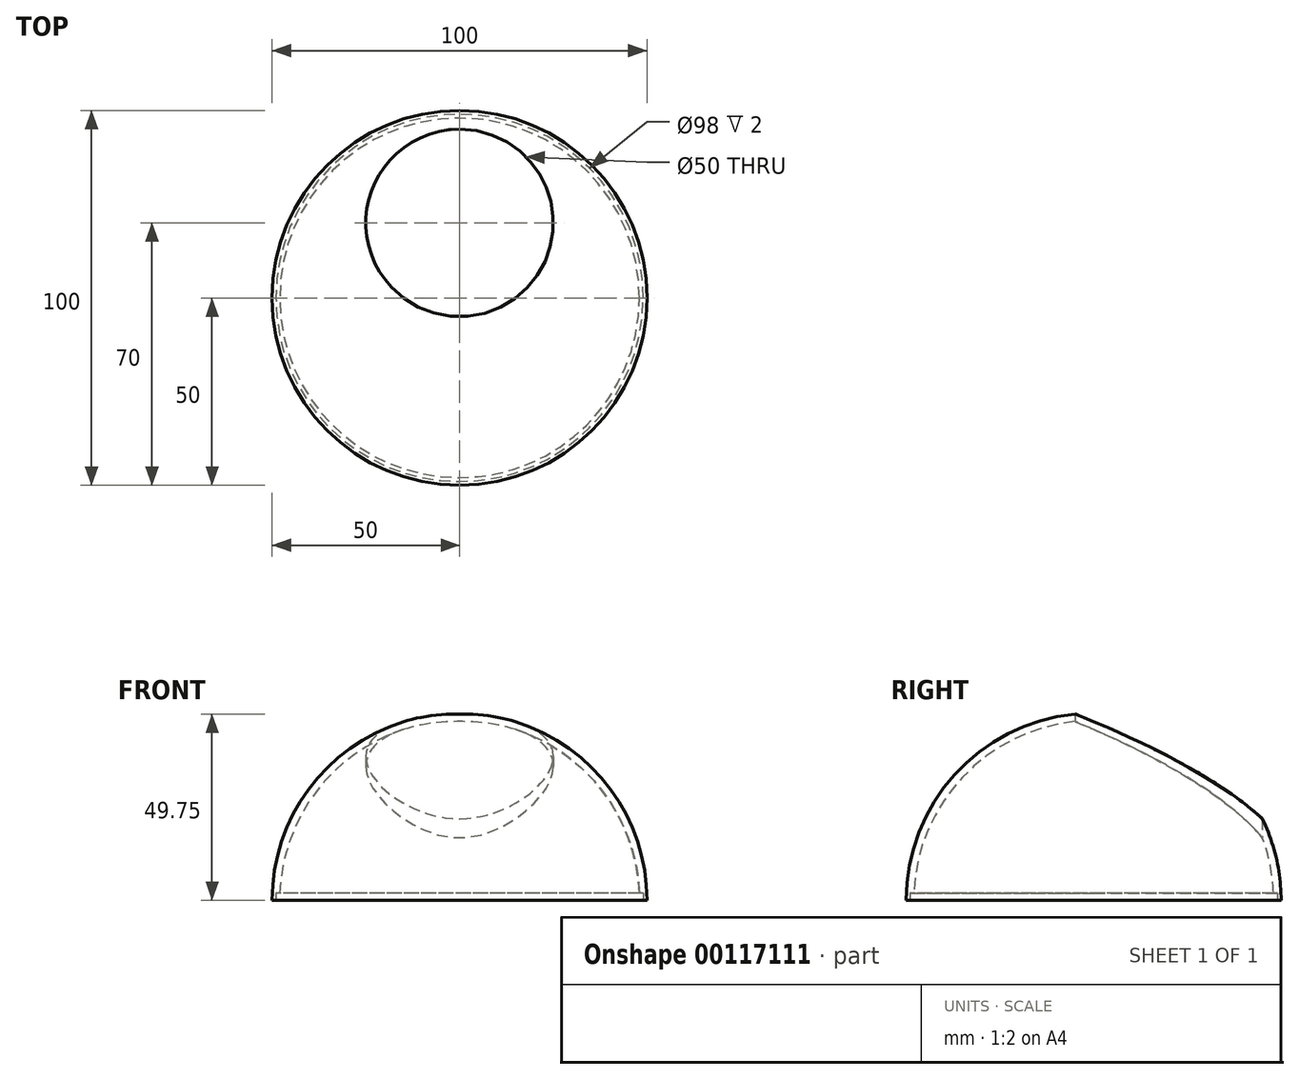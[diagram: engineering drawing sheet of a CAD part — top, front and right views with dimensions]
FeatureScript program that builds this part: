
annotation { "Feature Type Name" : "Feature", "Feature Type Description" : "" }
export const myFeature = defineFeature(function(context is Context, id is Id, definition is map)
    precondition{}
    {
        {
            var Q0;
            Q0=qCreatedBy(makeId("Front.planeOp"),FACE);
            var sketch = newSketch(context, id + "F0", { "sketchPlane" : qUnion([Q0])});
            skLineSegment(sketch, "E0.bottom", {"start": v(0, 0) * mm, "end": v(50, 0) * mm});
            skLineSegment(sketch, "E0.left", {"start": v(0, 0) * mm, "end": v(0, 50) * mm});
            skArc(sketch, "E1", {"start": v(0, 50) * mm, "mid": v(35.36, 35.36) * mm, "end": v(50, 0) * mm});
            skSolve(sketch);
        }
        {
            var Q0;
            Q0=qSketchRegion(id+"F0",true);
            var Q1;
            Q1=makeQuery(id+"F0.imprint","IMPRINT",FACE,{"disambiguationData":[TD([[makeQuery(id+"F0.imprint","IMPRINT",EDGE,{"derivedFrom":sQuery(id+"F0.wireOp",EDGE,"E0.bottom")}),1.0]])]});
            var Q2;
            Q2=sQuery(id+"F0.wireOp",EDGE,"E0.left");
            revolve(context, id + "F1", {"entities" : qUnion([Q0, Q1]), "axis" : qUnion([Q2]), "revolveType" : RevolveType.FULL});
        }
        {
            var Q0;
            Q0=makeQuery(id+"F1.opRevolve","SWEPT_FACE",FACE,{"disambiguationData":[OSD([sQuery(id+"F0.wireOp",EDGE,"E0.bottom")])]});
            shell(context, id + "F2", {"entities" : qUnion([Q0]), "thickness" : 2 * mm});
        }
        {
            var Q0;
            Q0=qCreatedBy(makeId("Top.planeOp"),FACE);
            var sketch = newSketch(context, id + "F3", { "sketchPlane" : qUnion([Q0])});
            skCircle(sketch, "E2", {"center": v(0, 0) * mm, "radius": 49 * mm});
            skSolve(sketch);
        }
        {
            var Q0;
            Q0=qSketchRegion(id+"F3",true);
            extrude(context, id + "F4", {"entities" : qUnion([Q0]), "operationType" : NewBodyOperationType.REMOVE, "depth" : 2 * mm});
        }
        {
            var Q0;
            Q0=qCreatedBy(makeId("Top.planeOp"),FACE);
            var sketch = newSketch(context, id + "F5", { "sketchPlane" : qUnion([Q0])});
            skCircle(sketch, "E3", {"center": v(0, 20) * mm, "radius": 25 * mm});
            skSolve(sketch);
        }
        {
            var Q0;
            Q0=qSketchRegion(id+"F5",true);
            extrude(context, id + "F6", {"entities" : qUnion([Q0]), "operationType" : NewBodyOperationType.REMOVE, "endBound" : BoundingType.THROUGH_ALL, "depth" : 25 * mm});
        }
    });
